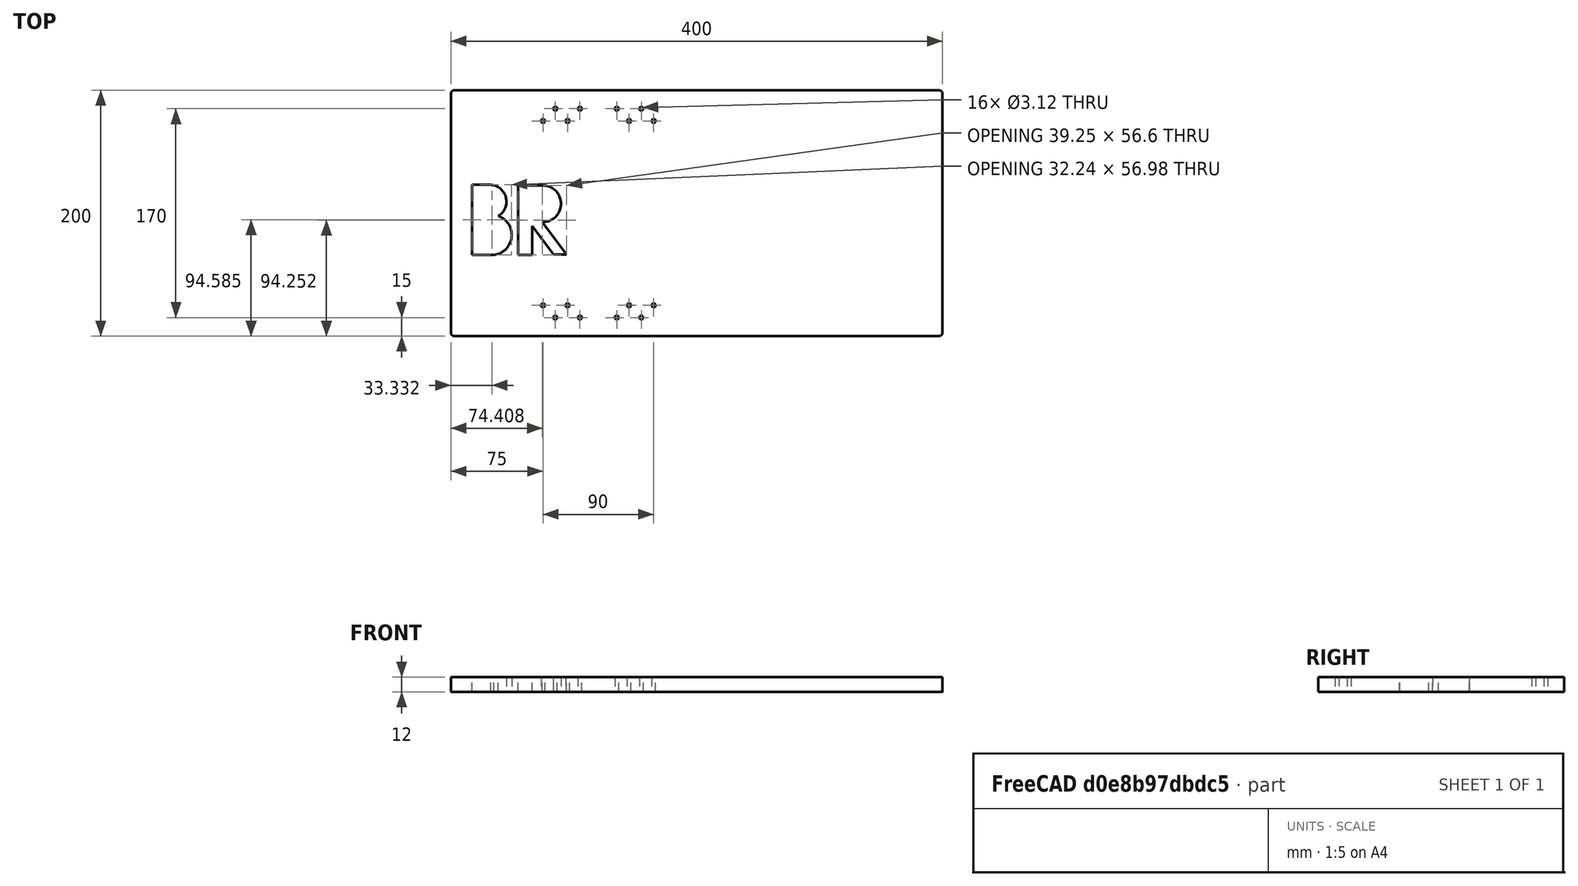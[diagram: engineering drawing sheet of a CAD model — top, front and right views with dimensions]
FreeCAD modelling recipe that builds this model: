
FCSTD DOCUMENT  (FreeCAD 0.19R24276 (Git))
Label: Osnovanie_200x400x12_H12_BR
License: All rights reserved
LicenseURL: http://en.wikipedia.org/wiki/All_rights_reserved
objects: Sketcher::SketchObject×1, PartDesign::Pad×1, PartDesign::Fillet×1, PartDesign::Body×1
note: 6 computed .brp shape members not serialized (recipe doc carries the construction recipe); baked Part::Feature solids carry a one-line shape summary decoded from their .brp

FEATURE [Sketcher::SketchObject] Sketch  label="Sketch_200x400"
  FullyConstrained = false
  MapMode = 5
  Support = -> [XY_Plane]
  sketch-geometry (48):
    g0: LineSegment StartX=0 StartY=0 StartZ=0 EndX=400 EndY=0 EndZ=0
    g1: LineSegment StartX=400 StartY=0 StartZ=0 EndX=400 EndY=200 EndZ=0
    g2: LineSegment StartX=400 StartY=200 StartZ=0 EndX=0 EndY=200 EndZ=0
    g3: LineSegment StartX=0 StartY=200 StartZ=0 EndX=0 EndY=0 EndZ=0
    g4: LineSegment StartX=0 StartY=100 StartZ=0 EndX=400 EndY=100 EndZ=0
    g5: Circle CenterX=120 CenterY=100 CenterZ=0 NormalX=0 NormalY=0 NormalZ=1 AngleXU=0 Radius=110
    g6: LineSegment StartX=120 StartY=100 StartZ=0 EndX=120 EndY=0 EndZ=0
    g7: LineSegment StartX=55 StartY=0 StartZ=0 EndX=185 EndY=0 EndZ=0
    g8: LineSegment StartX=185 StartY=0 StartZ=0 EndX=185 EndY=40 EndZ=0
    g9: LineSegment StartX=185 StartY=40 StartZ=0 EndX=55 EndY=40 EndZ=0
    g10: LineSegment StartX=55 StartY=40 StartZ=0 EndX=55 EndY=0 EndZ=0
    g11: LineSegment StartX=55 StartY=25 StartZ=0 EndX=185 EndY=25 EndZ=0
    g12: LineSegment StartX=55 StartY=15 StartZ=0 EndX=185 EndY=15 EndZ=0
    g13: Circle CenterX=85 CenterY=15 CenterZ=0 NormalX=0 NormalY=0 NormalZ=1 AngleXU=0 Radius=1.5625
    g14: Circle CenterX=105 CenterY=15 CenterZ=0 NormalX=0 NormalY=0 NormalZ=1 AngleXU=0 Radius=1.5625
    g15: Circle CenterX=75 CenterY=25 CenterZ=0 NormalX=0 NormalY=0 NormalZ=1 AngleXU=0 Radius=1.5625
    g16: Circle CenterX=95 CenterY=25 CenterZ=0 NormalX=0 NormalY=0 NormalZ=1 AngleXU=0 Radius=1.5625
    g17: Circle CenterX=155 CenterY=15 CenterZ=0 NormalX=0 NormalY=0 NormalZ=1 AngleXU=0 Radius=1.5625
    g18: Circle CenterX=135 CenterY=15 CenterZ=0 NormalX=0 NormalY=0 NormalZ=1 AngleXU=0 Radius=1.5625
    g19: Circle CenterX=145 CenterY=25 CenterZ=0 NormalX=0 NormalY=0 NormalZ=1 AngleXU=0 Radius=1.5625
    g20: Circle CenterX=165 CenterY=25 CenterZ=0 NormalX=0 NormalY=0 NormalZ=1 AngleXU=0 Radius=1.5625
    g21: LineSegment StartX=55 StartY=200 StartZ=0 EndX=185 EndY=200 EndZ=0
    g22: LineSegment StartX=185 StartY=200 StartZ=0 EndX=185 EndY=160 EndZ=0
    g23: LineSegment StartX=185 StartY=160 StartZ=0 EndX=55 EndY=160 EndZ=0
    g24: LineSegment StartX=55 StartY=160 StartZ=0 EndX=55 EndY=200 EndZ=0
    g25: LineSegment StartX=55 StartY=175 StartZ=0 EndX=185 EndY=175 EndZ=0
    g26: LineSegment StartX=55 StartY=185 StartZ=0 EndX=185 EndY=185 EndZ=0
    g27: Circle CenterX=85 CenterY=185 CenterZ=0 NormalX=0 NormalY=0 NormalZ=1 AngleXU=0 Radius=1.5625
    g28: Circle CenterX=105 CenterY=185 CenterZ=0 NormalX=0 NormalY=0 NormalZ=1 AngleXU=0 Radius=1.5625
    g29: Circle CenterX=75 CenterY=175 CenterZ=0 NormalX=0 NormalY=0 NormalZ=1 AngleXU=0 Radius=1.5625
    g30: Circle CenterX=95 CenterY=175 CenterZ=0 NormalX=0 NormalY=0 NormalZ=1 AngleXU=0 Radius=1.5625
    g31: Circle CenterX=155 CenterY=185 CenterZ=0 NormalX=0 NormalY=0 NormalZ=1 AngleXU=0 Radius=1.5625
    g32: Circle CenterX=135 CenterY=185 CenterZ=0 NormalX=0 NormalY=0 NormalZ=1 AngleXU=0 Radius=1.5625
    g33: Circle CenterX=145 CenterY=175 CenterZ=0 NormalX=0 NormalY=0 NormalZ=1 AngleXU=0 Radius=1.5625
    g34: Circle CenterX=165 CenterY=175 CenterZ=0 NormalX=0 NormalY=0 NormalZ=1 AngleXU=0 Radius=1.5625
    g35: LineSegment StartX=17.2115 StartY=123.076 StartZ=0 EndX=32.4213 EndY=123.076 EndZ=0
    g36: LineSegment StartX=17.2115 StartY=66.0931 StartZ=0 EndX=17.2115 EndY=123.076 EndZ=0
    g37: ArcOfCircle CenterX=33.2127 CenterY=82.3058 CenterZ=0 NormalX=0 NormalY=0 NormalZ=1 AngleXU=0 Radius=16.3376 StartAngle=4.83607 EndAngle=7.51129
    g38: LineSegment StartX=66.2608 StartY=65.953 StartZ=0 EndX=54.7814 EndY=65.953 EndZ=0
    g39: LineSegment StartX=54.7814 StartY=65.953 StartZ=0 EndX=54.7814 EndY=122.551 EndZ=0
    g40: LineSegment StartX=66.2608 StartY=89.5965 StartZ=0 EndX=83.78 EndY=66.3383 EndZ=0
    g41: LineSegment StartX=83.78 StartY=66.3383 StartZ=0 EndX=94.034 EndY=66.3383 EndZ=0
    g42: LineSegment StartX=94.034 StartY=66.3383 StartZ=0 EndX=74.3517 EndY=92.7656 EndZ=0
    g43: ArcOfCircle CenterX=31.5368 CenterY=109.389 CenterZ=0 NormalX=0 NormalY=0 NormalZ=1 AngleXU=0 Radius=13.7159 StartAngle=5.26209 EndAngle=7.78945
    g44: LineSegment StartX=66.2608 StartY=89.5965 StartZ=0 EndX=66.2608 EndY=65.953 EndZ=0
    g45: ArcOfCircle CenterX=74.7159 CenterY=107.658 CenterZ=0 NormalX=0 NormalY=0 NormalZ=1 AngleXU=0 Radius=14.8972 StartAngle=4.68794 EndAngle=7.8784
    g46: LineSegment StartX=35.2283 StartY=66.0931 StartZ=0 EndX=17.2115 EndY=66.0931 EndZ=0
    g47: LineSegment StartX=74.3522 StartY=122.551 StartZ=0 EndX=54.7814 EndY=122.551 EndZ=0
  constraints (100):
    c: Coincident(g0,g1)
    c: Coincident(g1,g2)
    c: Coincident(g2,g3)
    c: Coincident(g3,g0)
    c: Horizontal(g0)
    c: Horizontal(g2)
    c: Vertical(g1)
    c: Vertical(g3)
    c: Coincident(g0,g-1)
    c: DistanceY(g1,g1) = 200
    c: DistanceX(g0,g0) = 400
    c: Horizontal(g4)
    c: Symmetric(g0,g1,g4)
    c: DistanceX(g0,g6) = 120
    c: PointOnObject(g6,g4)
    c: Coincident(g5,g6)
    c: Diameter(g5) = 220
    c: Coincident(g7,g8)
    c: Coincident(g8,g9)
    c: Coincident(g9,g10)
    c: Coincident(g10,g7)
    c: Horizontal(g7)
    c: Horizontal(g9)
    c: Vertical(g8)
    c: Vertical(g10)
    c: PointOnObject(g7,g0)
    c: DistanceX(g9,g9) = 130
    c: Symmetric(g7,g7,g6)
    c: DistanceY(g8,g8) = 40
    c: PointOnObject(g12,g8)
    c: PointOnObject(g11,g8)
    c: PointOnObject(g11,g10)
    c: PointOnObject(g12,g10)
    c: DistanceY(g7,g12) = 15
    c: DistanceY(g7,g11) = 25
    c: Horizontal(g11)
    c: Horizontal(g12)
    c: PointOnObject(g13,g12)
    c: PointOnObject(g14,g12)
    c: PointOnObject(g15,g11)
    c: PointOnObject(g16,g11)
    c: Equal(g13,g14)
    c: Equal(g14,g15)
    c: Equal(g15,g16)
    c: Diameter(g14) = 3.125
    c: DistanceX(g9,g15) = 20
    c: DistanceX(g15,g16) = 20
    c: DistanceX(g13,g14) = 20
    c: DistanceX(g15,g13) = 10
    c: Equal(g17,g18)
    c: Equal(g18,g20)
    c: Equal(g20,g19)
    c: Diameter(g18) = 3.125
    c: Coincident(g21,g22)
    c: Coincident(g22,g23)
    c: Coincident(g23,g24)
    c: Coincident(g24,g21)
    c: Horizontal(g21)
    c: Horizontal(g23)
    c: Vertical(g22)
    c: Vertical(g24)
    c: PointOnObject(g26,g22)
    c: PointOnObject(g25,g22)
    c: PointOnObject(g25,g24)
    c: PointOnObject(g26,g24)
    c: Horizontal(g25)
    c: Horizontal(g26)
    c: PointOnObject(g27,g26)
    c: PointOnObject(g28,g26)
    c: PointOnObject(g29,g25)
    c: PointOnObject(g30,g25)
    c: Equal(g27,g28)
    c: Equal(g28,g29)
    c: Equal(g29,g30)
    c: Diameter(g28) = 3.125
    c: Equal(g31,g32)
    c: Equal(g32,g34)
    c: Equal(g34,g33)
    c: Diameter(g32) = 3.125
    c: PointOnObject(g4,g3)
    c: Coincident(g36,g35)
    c: Horizontal(g35)
    c: Vertical(g36)
    c: Coincident(g44,g38)
    c: Coincident(g38,g39)
    c: Horizontal(g38)
    c: Vertical(g39)
    c: Coincident(g41,g40)
    c: Horizontal(g41)
    c: Coincident(g42,g41)
    c: Coincident(g35,g43)
    c: Coincident(g37,g43)
    c: Coincident(g44,g40)
    c: Coincident(g45,g42)
    c: Coincident(g46,g37)
    c: Coincident(g46,g36)
    c: Horizontal(g46)
    c: Coincident(g47,g45)
    c: Coincident(g47,g39)
    c: Horizontal(g47)
FEATURE [PartDesign::Pad] Pad  label="Pad_h12"
  Direction = (1,1,1)
  Length = 12
  Length2 = 100
  Profile = -> Sketch
  Type = 0
FEATURE [PartDesign::Fillet] Fillet
  Base = -> Pad [Edge1,Edge2,Edge5,Edge8]
  BaseFeature = -> Pad
  Radius = 3
  SupportTransform = false
FEATURE [PartDesign::Body] Body
  Group = -> [Sketch,Pad,Fillet]
  Origin = -> Origin
  Tip = -> Fillet
